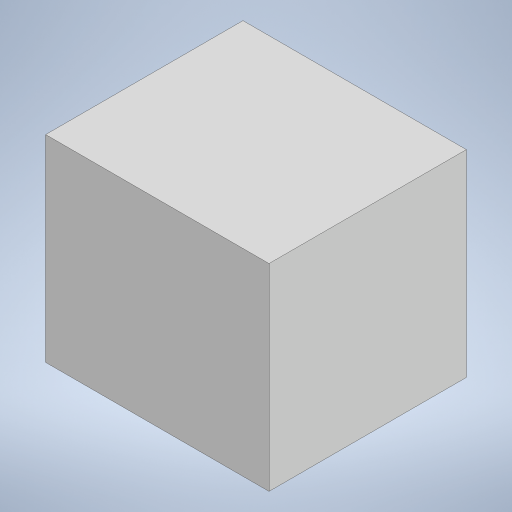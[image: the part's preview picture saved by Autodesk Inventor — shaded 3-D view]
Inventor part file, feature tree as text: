
AUTODESK INVENTOR PART (.ipt)
format: ipt  version: 2023 (Build 270158000, 158)  size: 160,768 bytes
history: native  units: mm
features: extrude x1, sketch x1
ambient origin geometry x8: Origin, YZ Plane, XZ Plane, XY Plane, X Axis, Y Axis, Z Axis, Center Point
bodies: Volumenkörper1 (feature_tree)
feature tree (2):
  extrude  "Extrusion1"  Depth=26.5mm
  sketch  "Skizze1"  dims[d0=26.5mm d1=26.5mm d2=30.0mm d3=0.0mm]
